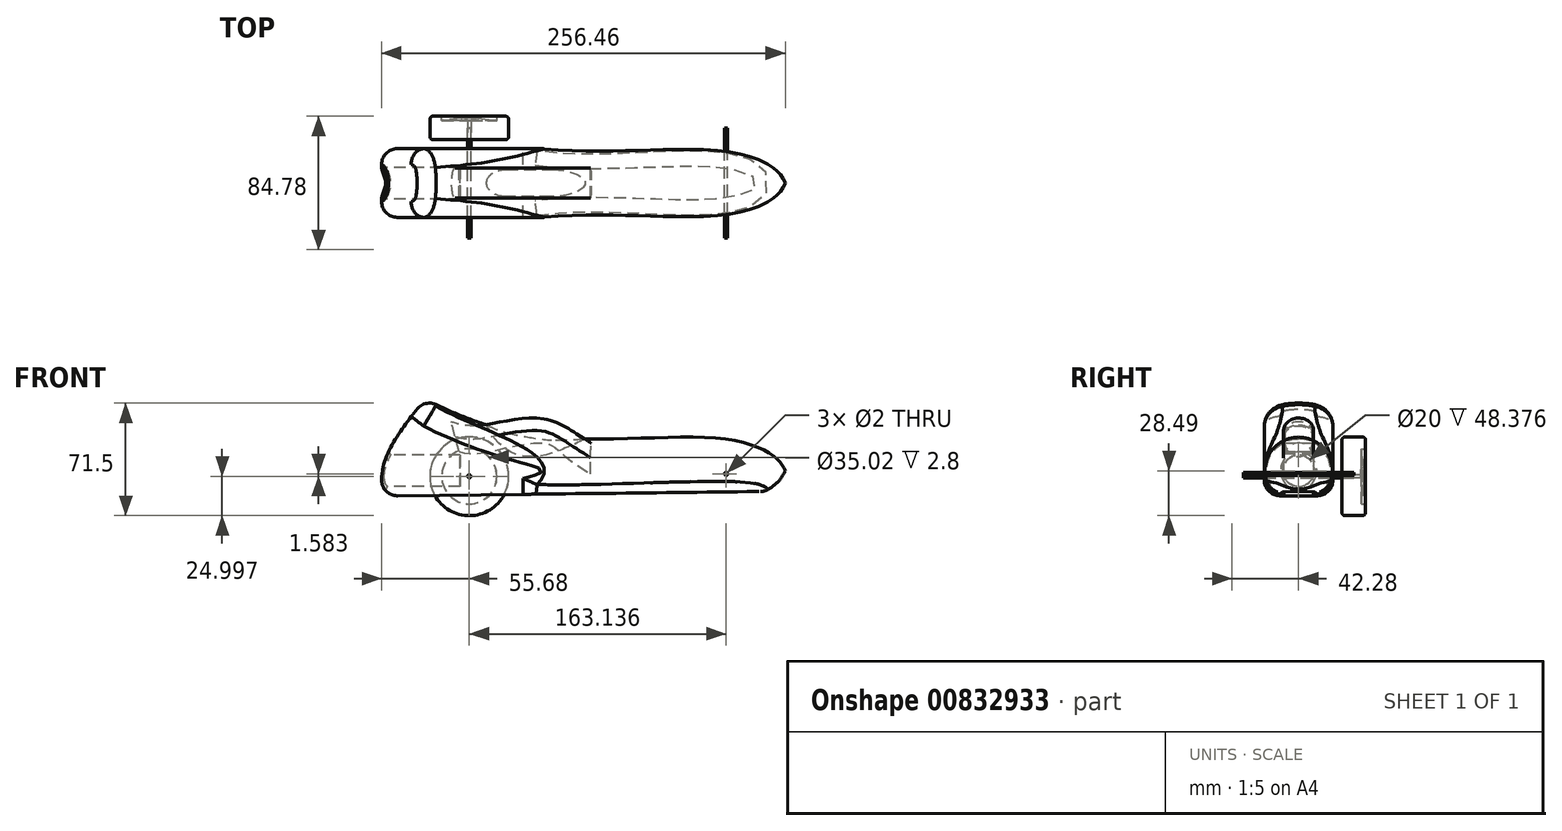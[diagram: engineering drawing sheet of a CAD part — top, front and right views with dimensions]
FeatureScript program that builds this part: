
annotation { "Feature Type Name" : "Feature", "Feature Type Description" : "" }
export const myFeature = defineFeature(function(context is Context, id is Id, definition is map)
    precondition{}
    {
        {
            var Q0;
            Q0=qCreatedBy(makeId("Front.planeOp"),FACE);
            var sketch = newSketch(context, id + "F0", { "sketchPlane" : qUnion([Q0])});
            skLineSegment(sketch, "E0", {"start": v(-118.32, 0) * mm, "end": v(131.68, 0) * mm, "construction": true});
            skFitSpline(sketch, "E1", {"points": [v(131.68, 0) * mm, v(126.03, 7.94) * mm, v(93, 20.22) * mm, v(-29.78, 22.76) * mm, v(-128.5, 62.65) * mm], "startDerivative": vector(-40.38, 77.18) * mm, "endDerivative": vector(-267.3, 151.76) * mm});
            skLineSegment(sketch, "E2", {"start": v(-128.5, 62.65) * mm, "end": v(-128.5, 0) * mm});
            skLineSegment(sketch, "E3", {"start": v(-128.5, 0) * mm, "end": v(131.68, 0) * mm});
            skSolve(sketch);
        }
        {
            var Q0;
            Q0 = qSketchRegion(id + "F0", true);
            var Q1;
            Q1=sQuery(id+"F0.wireOp",EDGE,"E3");
            revolve(context, id + "F1", {"surfaceOperationType" : NewSurfaceOperationType.NEW, "entities" : qUnion([Q0]), "axis" : qUnion([Q1]), "revolveType" : RevolveType.FULL});
        }
        {
            var Q0;
            Q0=qCreatedBy(makeId("Front.planeOp"),FACE);
            var sketch = newSketch(context, id + "F2", { "sketchPlane" : qUnion([Q0])});
            skLineSegment(sketch, "E4", {"start": v(129, -13) * mm, "end": v(-152.67, -16.28) * mm});
            skLineSegment(sketch, "E5", {"start": v(-152.67, -16.28) * mm, "end": v(-151.96, -77.92) * mm});
            skLineSegment(sketch, "E6", {"start": v(-151.96, -77.92) * mm, "end": v(124.08, -74.71) * mm});
            skLineSegment(sketch, "E7", {"start": v(124.08, -74.71) * mm, "end": v(129, -13) * mm});
            skSolve(sketch);
        }
        {
            var Q0;
            Q0=makeQuery(id+"F2.imprint","IMPRINT",FACE,{"disambiguationData":[TD([[makeQuery(id+"F2.imprint","IMPRINT",EDGE,{"derivedFrom":sQuery(id+"F2.wireOp",EDGE,"E4")}),1.0]])]});
            extrude(context, id + "F3", {"entities" : qUnion([Q0]), "operationType" : NewBodyOperationType.REMOVE, "endBound" : BoundingType.THROUGH_ALL, "oppositeDirection" : true, "depth" : 25 * mm, "offsetDistance" : 25 * mm, "hasSecondDirection" : true, "secondDirectionBound" : BoundingType.THROUGH_ALL, "secondDirectionOppositeDirection" : false, "secondDirectionDepth" : 25 * mm});
        }
        {
            var Q0;
            Q0=qCreatedBy(makeId("Right.planeOp"),FACE);
            var sketch = newSketch(context, id + "F4", { "sketchPlane" : qUnion([Q0])});
            skLineSegment(sketch, "E8", {"start": v(21.79, -20.57) * mm, "end": v(21.79, 59.86) * mm});
            skLineSegment(sketch, "E9", {"start": v(21.79, 59.86) * mm, "end": v(72.66, 59.86) * mm});
            skLineSegment(sketch, "E10", {"start": v(72.66, 59.86) * mm, "end": v(72.66, -20.57) * mm});
            skLineSegment(sketch, "E11", {"start": v(72.66, -20.57) * mm, "end": v(21.46, -20.57) * mm});
            skLineSegment(sketch, "E12.MirrorCS", {"start": v(-21.79, -20.57) * mm, "end": v(-21.79, 59.86) * mm});
            skLineSegment(sketch, "E13.MirrorCS", {"start": v(-21.79, 59.86) * mm, "end": v(-72.66, 59.86) * mm});
            skLineSegment(sketch, "E14.MirrorCS", {"start": v(-72.66, 59.86) * mm, "end": v(-72.66, -20.57) * mm});
            skLineSegment(sketch, "E15.MirrorCS", {"start": v(-72.66, -20.57) * mm, "end": v(-21.46, -20.57) * mm});
            skSolve(sketch);
        }
        {
            var Q0;
            {var subQ0=sQuery(id+"F4.wireOp",EDGE,"E12.MirrorCS");Q0=makeQuery(id+"F4.imprint","IMPRINT",FACE,{"disambiguationData":[TD([[makeQuery(id+"F4.imprint","IMPRINT",EDGE,{"derivedFrom":subQ0}),1.0]])]});}
            var Q1;
            {var subQ0=sQuery(id+"F4.wireOp",EDGE,"E8");Q1=makeQuery(id+"F4.imprint","IMPRINT",FACE,{"disambiguationData":[TD([[makeQuery(id+"F4.imprint","IMPRINT",EDGE,{"derivedFrom":subQ0}),-1.0]])]});}
            extrude(context, id + "F5", {"entities" : qUnion([Q0, Q1]), "operationType" : NewBodyOperationType.REMOVE, "endBound" : BoundingType.THROUGH_ALL, "oppositeDirection" : true, "depth" : 25 * mm, "offsetDistance" : 25 * mm});
        }
        {
            var Q0;
            Q0=makeQuery(id+"F5.boolean.opBoolean","INTERSECT",EDGE,{"derivedFrom":[makeQuery(id+"F1.opRevolve","SWEPT_FACE",FACE,{"disambiguationData":[OSD([sQuery(id+"F0.wireOp",EDGE,"E1")])]}),makeQuery(id+"F5.opExtrude","SWEPT_FACE",FACE,{"disambiguationData":[OSD([sQuery(id+"F4.wireOp",EDGE,"E12.MirrorCS")])]})]});
            var Q1;
            Q1=makeQuery(id+"F5.boolean.opBoolean","INTERSECT",EDGE,{"derivedFrom":[makeQuery(id+"F1.opRevolve","SWEPT_FACE",FACE,{"disambiguationData":[OSD([sQuery(id+"F0.wireOp",EDGE,"E1")])]}),makeQuery(id+"F5.opExtrude","SWEPT_FACE",FACE,{"disambiguationData":[OSD([sQuery(id+"F4.wireOp",EDGE,"E8")])]})]});
            fillet(context, id + "F6", {"entities" : qUnion([Q0, Q1]), "radius" : 15 * mm, "tangentPropagation" : true, "allowEdgeOverflow" : false});
        }
        {
            var Q0;
            Q0=qCreatedBy(makeId("Front.planeOp"),FACE);
            var sketch = newSketch(context, id + "F7", { "sketchPlane" : qUnion([Q0])});
            skFitSpline(sketch, "E16", {"points": [v(-121.86, -24.45) * mm, v(-123.5, 3.78) * mm, v(-90.97, 53.08) * mm], "startDerivative": vector(-16.07, 66.09) * mm, "endDerivative": vector(72.48, 87.66) * mm});
            skLineSegment(sketch, "E17", {"start": v(-90.97, 53.08) * mm, "end": v(-135.15, 76.81) * mm});
            skLineSegment(sketch, "E18", {"start": v(-135.15, 76.81) * mm, "end": v(-154.59, -23.22) * mm});
            skLineSegment(sketch, "E19", {"start": v(-154.59, -23.22) * mm, "end": v(-122.27, -35.5) * mm});
            skLineSegment(sketch, "E20", {"start": v(-122.27, -35.5) * mm, "end": v(-121.86, -24.45) * mm});
            skSolve(sketch);
        }
        {
            var Q0;
            Q0=makeQuery(id+"F7.imprint","IMPRINT",FACE,{"disambiguationData":[TD([[makeQuery(id+"F7.imprint","IMPRINT",EDGE,{"derivedFrom":sQuery(id+"F7.wireOp",EDGE,"E16")}),1.0]])]});
            extrude(context, id + "F8", {"entities" : qUnion([Q0]), "operationType" : NewBodyOperationType.REMOVE, "endBound" : BoundingType.THROUGH_ALL, "oppositeDirection" : true, "depth" : 25 * mm, "offsetDistance" : 25 * mm, "hasSecondDirection" : true, "secondDirectionBound" : BoundingType.THROUGH_ALL, "secondDirectionOppositeDirection" : false, "secondDirectionDepth" : 25 * mm});
        }
        {
            var Q0;
            Q0=makeQuery(id+"F8.boolean.opBoolean","INTERSECT",EDGE,{"derivedFrom":[makeQuery(id+"F5.boolean.opBoolean","COPY",FACE,{"derivedFrom":makeQuery(id+"F5.opExtrude","SWEPT_FACE",FACE,{"disambiguationData":[OSD([sQuery(id+"F4.wireOp",EDGE,"E12.MirrorCS")])]})}),makeQuery(id+"F8.opExtrude","SWEPT_FACE",FACE,{"disambiguationData":[OSD([sQuery(id+"F7.wireOp",EDGE,"E16")])]})]});
            fillet(context, id + "F9", {"entities" : qUnion([Q0]), "radius" : 10 * mm, "tangentPropagation" : true, "allowEdgeOverflow" : false});
        }
        {
            var Q0;
            Q0=makeQuery(id+"F5.boolean.opBoolean","INTERSECT",EDGE,{"derivedFrom":[makeQuery(id+"F3.boolean.opBoolean","COPY",FACE,{"derivedFrom":makeQuery(id+"F3.opExtrude","SWEPT_FACE",FACE,{"disambiguationData":[OSD([sQuery(id+"F2.wireOp",EDGE,"E4")])]})}),makeQuery(id+"F5.opExtrude","SWEPT_FACE",FACE,{"disambiguationData":[OSD([sQuery(id+"F4.wireOp",EDGE,"E8")])]})]});
            fillet(context, id + "F10", {"entities" : qUnion([Q0]), "radius" : 10 * mm, "tangentPropagation" : true, "allowEdgeOverflow" : false});
        }
        {
            var Q0;
            Q0=qCreatedBy(makeId("Right.planeOp"),FACE);
            cPlane(context, id + "F11", {"entities" : qUnion([Q0]), "cplaneType" : CPlaneType.OFFSET, "offset" : 124.9 * mm, "oppositeDirection" : true, "width" : 150 * mm, "height" : 150 * mm});
        }
        {
            var Q0;
            Q0=qCreatedBy(id+"F11.planeOp",FACE);
            var sketch = newSketch(context, id + "F12", { "sketchPlane" : qUnion([Q0])});
            skCircle(sketch, "E21", {"center": v(0, 0) * mm, "radius": 10 * mm});
            skSolve(sketch);
        }
        {
            var Q0;
            Q0=makeQuery(id+"F12.imprint","IMPRINT",FACE,{"disambiguationData":[TD([[makeQuery(id+"F12.imprint","IMPRINT",EDGE,{"derivedFrom":sQuery(id+"F12.wireOp",EDGE,"E21")}),1.0]])]});
            extrude(context, id + "F13", {"entities" : qUnion([Q0]), "operationType" : NewBodyOperationType.REMOVE, "depth" : 50 * mm, "offsetDistance" : 25 * mm});
        }
        {
            var Q0;
            Q0=makeQuery(id+"F13.boolean.opBoolean","INTERSECT",EDGE,{"derivedFrom":[makeQuery(id+"F8.boolean.opBoolean","COPY",FACE,{"derivedFrom":makeQuery(id+"F8.opExtrude","SWEPT_FACE",FACE,{"disambiguationData":[OSD([sQuery(id+"F7.wireOp",EDGE,"E16")])]})}),makeQuery(id+"F13.opExtrude","SWEPT_FACE",FACE,{"disambiguationData":[OSD([sQuery(id+"F12.wireOp",EDGE,"E21")])]})]});
            var Q1;
            Q1=makeQuery(id+"F13.boolean.opBoolean","INTERSECT",EDGE,{"derivedFrom":[makeQuery(id+"F10.opFillet","BLEND_FACE",FACE,{"disambiguationData":[OSD([sQuery(id+"F2.wireOp",EDGE,"E4"),sQuery(id+"F7.wireOp",EDGE,"E16")])]}),makeQuery(id+"F13.opExtrude","SWEPT_FACE",FACE,{"disambiguationData":[OSD([sQuery(id+"F12.wireOp",EDGE,"E21")])]})]});
            chamfer(context, id + "F14", {"entities" : qUnion([Q0, Q1]), "width" : 1.5 * mm, "tangentPropagation" : true});
        }
        {
            var Q0;
            Q0=qCreatedBy(makeId("Front.planeOp"),FACE);
            var sketch = newSketch(context, id + "F15", { "sketchPlane" : qUnion([Q0])});
            skLineSegment(sketch, "E22", {"start": v(-81.16, -3.61) * mm, "end": v(140.1, -1.46) * mm, "construction": true});
            skCircle(sketch, "E23", {"center": v(94.04, -1.91) * mm, "radius": 1 * mm});
            skCircle(sketch, "E24", {"center": v(-69.1, -3.5) * mm, "radius": 1 * mm});
            skSolve(sketch);
        }
        {
            var Q0;
            Q0 = qSketchRegion(id + "F15", true);
            extrude(context, id + "F16", {"entities" : qUnion([Q0]), "operationType" : NewBodyOperationType.REMOVE, "endBound" : BoundingType.THROUGH_ALL, "depth" : 25 * mm, "offsetDistance" : 25 * mm, "hasSecondDirection" : true, "secondDirectionBound" : BoundingType.THROUGH_ALL, "secondDirectionOppositeDirection" : true, "secondDirectionDepth" : 25 * mm});
        }
        {
            var Q0;
            Q0 = qSketchRegion(id + "F15", true);
            extrude(context, id + "F17", {"entities" : qUnion([Q0]), "depth" : 35 * mm, "offsetDistance" : 25 * mm, "hasSecondDirection" : true, "secondDirectionOppositeDirection" : true, "secondDirectionDepth" : 35 * mm});
        }
        {
            var Q0;
            Q0=makeQuery(id+"F17.opExtrude","CAP_FACE",FACE,{"disambiguationData":[OSD([sQuery(id+"F15.wireOp",EDGE,"E24")])],"isStart":true});
            var sketch = newSketch(context, id + "F18", { "sketchPlane" : qUnion([Q0])});
            skCircle(sketch, "E25", {"center": v(69.1, -3.5) * mm, "radius": 25 * mm});
            skSolve(sketch);
        }
        {
            var Q0;
            Q0=makeQuery(id+"F18.imprint","IMPRINT",FACE,{"disambiguationData":[TD([[makeQuery(id+"F18.imprint","IMPRINT",EDGE,{"derivedFrom":sQuery(id+"F18.wireOp",EDGE,"E25")}),1.0]])]});
            extrude(context, id + "F19", {"entities" : qUnion([Q0]), "depth" : 15 * mm, "offsetDistance" : 25 * mm, "symmetric" : true});
        }
        {
            var Q0;
            Q0=makeQuery(id+"F19.opExtrude","CAP_FACE",FACE,{"disambiguationData":[OSD([sQuery(id+"F15.wireOp",EDGE,"E24"),sQuery(id+"F18.wireOp",EDGE,"E25")])],"isStart":false});
            var sketch = newSketch(context, id + "F20", { "sketchPlane" : qUnion([Q0])});
            skCircle(sketch, "E26", {"center": v(69.1, -3.5) * mm, "radius": 17.5 * mm});
            skSolve(sketch);
        }
        {
            var Q0;
            Q0=makeQuery(id+"F20.imprint","IMPRINT",FACE,{"disambiguationData":[TD([[makeQuery(id+"F20.imprint","IMPRINT",EDGE,{"derivedFrom":sQuery(id+"F20.wireOp",EDGE,"E26")}),1.0]])]});
            extrude(context, id + "F21", {"entities" : qUnion([Q0]), "operationType" : NewBodyOperationType.REMOVE, "oppositeDirection" : true, "depth" : 2.8 * mm, "offsetDistance" : 25 * mm});
        }
        {
            var Q0;
            Q0=makeQuery(id+"F21.boolean.opBoolean","COPY",EDGE,{"derivedFrom":makeQuery(id+"F21.opExtrude","CAP_EDGE",EDGE,{"disambiguationData":[OSD([sQuery(id+"F20.wireOp",EDGE,"E26")])],"isStart":true})});
            var Q1;
            Q1=makeQuery(id+"F19.opExtrude","CAP_EDGE",EDGE,{"disambiguationData":[OSD([sQuery(id+"F18.wireOp",EDGE,"E25")])],"isStart":false});
            var Q2;
            Q2=makeQuery(id+"F19.opExtrude","CAP_EDGE",EDGE,{"disambiguationData":[OSD([sQuery(id+"F18.wireOp",EDGE,"E25")])],"isStart":true});
            fillet(context, id + "F22", {"entities" : qUnion([Q0, Q1, Q2]), "radius" : 2 * mm, "tangentPropagation" : true, "allowEdgeOverflow" : false});
        }
        {
            var Q0;
            Q0=qCreatedBy(makeId("Top.planeOp"),FACE);
            cPlane(context, id + "F23", {"entities" : qUnion([Q0]), "cplaneType" : CPlaneType.OFFSET, "offset" : 3.5 * mm, "oppositeDirection" : true, "width" : 150 * mm, "height" : 150 * mm});
        }
        {
            var Q0;
            Q0=qCreatedBy(id+"F23.planeOp",FACE);
            var sketch = newSketch(context, id + "F24", { "sketchPlane" : qUnion([Q0])});
            skLineSegment(sketch, "E27", {"start": v(-51.54, 39.75) * mm, "end": v(-67.92, 41.8) * mm});
            skLineSegment(sketch, "E28", {"start": v(-68.3, 39.66) * mm, "end": v(-67.92, 41.8) * mm});
            skLineSegment(sketch, "E29", {"start": v(-68.3, 39.66) * mm, "end": v(-51.54, 39.75) * mm});
            skLineSegment(sketch, "E30", {"start": v(-69.06, 35.08) * mm, "end": v(-69.06, 45.18) * mm, "construction": true});
            skSolve(sketch);
        }
        {
            var Q0;
            Q0 = qSketchRegion(id + "F24", true);
            var Q1;
            Q1=sQuery(id+"F24.wireOp",EDGE,"E30");
            revolve(context, id + "F25", {"surfaceOperationType" : NewSurfaceOperationType.NEW, "entities" : qUnion([Q0]), "axis" : qUnion([Q1]), "revolveType" : RevolveType.FULL});
        }
        {
            var Q0;
            Q0=makeQuery(id+"F25.opRevolve","SWEPT_EDGE",EDGE,{"disambiguationData":[OSD([sQuery(id+"F24.wireOp",EDGE,"E27"),sQuery(id+"F24.wireOp",EDGE,"E28")])]});
            fillet(context, id + "F26", {"entities" : qUnion([Q0]), "radius" : 5 * mm, "tangentPropagation" : true, "allowEdgeOverflow" : false});
        }
        {
            var Q0;
            Q0=qCreatedBy(makeId("Front.planeOp"),FACE);
            var sketch = newSketch(context, id + "F27", { "sketchPlane" : qUnion([Q0])});
            skFitSpline(sketch, "E31", {"points": [v(12.04, 32.77) * mm, v(-25.2, 17.09) * mm, v(-43.84, 21.99) * mm, v(-57.56, 47.8) * mm], "startDerivative": vector(-100.83, -53.7) * mm, "endDerivative": vector(-34.57, 90.8) * mm});
            skSolve(sketch);
        }
        {
            var Q0;
            Q0=qCreatedBy(makeId("Right.planeOp"),FACE);
            var sketch = newSketch(context, id + "F28", { "sketchPlane" : qUnion([Q0])});
            skArc(sketch, "E32", {"start": v(-8.61, 26.84) * mm, "mid": v(0, 18.06) * mm, "end": v(8.61, 26.84) * mm});
            skLineSegment(sketch, "E33", {"start": v(-8.61, 26.84) * mm, "end": v(-8.37, 39.02) * mm});
            skLineSegment(sketch, "E34", {"start": v(8.61, 26.84) * mm, "end": v(8.37, 39) * mm});
            skLineSegment(sketch, "E35", {"start": v(8.37, 39) * mm, "end": v(-8.37, 39.02) * mm});
            skSolve(sketch);
        }
        {
            var Q0;
            Q0=makeQuery(id+"F28.imprint","IMPRINT",FACE,{"disambiguationData":[TD([[makeQuery(id+"F28.imprint","IMPRINT",EDGE,{"derivedFrom":sQuery(id+"F28.wireOp",EDGE,"E32")}),1.0]])]});
            var Q1;
            Q1=sQuery(id+"F27.wireOp",EDGE,"E31");
            sweep(context, id + "F29", {"operationType" : NewBodyOperationType.REMOVE, "profiles" : qUnion([Q0]), "path" : qUnion([Q1])});
        }
        {
            var Q0;
            Q0=qCreatedBy(makeId("Right.planeOp"),FACE);
            var sketch = newSketch(context, id + "F30", { "sketchPlane" : qUnion([Q0])});
            skArc(sketch, "E36", {"start": v(9.54, 13.44) * mm, "mid": v(0, 22.99) * mm, "end": v(-9.54, 13.44) * mm});
            skLineSegment(sketch, "E37", {"start": v(9.54, 13.44) * mm, "end": v(9.54, 3.35) * mm});
            skLineSegment(sketch, "E38", {"start": v(-9.54, 3.35) * mm, "end": v(-9.54, 13.44) * mm});
            skLineSegment(sketch, "E39", {"start": v(-9.54, 3.35) * mm, "end": v(9.54, 3.35) * mm});
            skSolve(sketch);
        }
        {
            var Q0;
            Q0=qCreatedBy(makeId("Front.planeOp"),FACE);
            var sketch = newSketch(context, id + "F31", { "sketchPlane" : qUnion([Q0])});
            skFitSpline(sketch, "E40", {"points": [v(8.14, 16.84) * mm, v(-4.5, 24.95) * mm, v(-26.35, 32.78) * mm, v(-65.37, 27.97) * mm, v(-80.35, 30.3) * mm], "startDerivative": vector(-58.37, 38.53) * mm, "endDerivative": vector(-61.48, 19.47) * mm});
            skSolve(sketch);
        }
        {
            var Q0;
            Q0=makeQuery(id+"F30.imprint","IMPRINT",FACE,{"disambiguationData":[TD([[makeQuery(id+"F30.imprint","IMPRINT",EDGE,{"derivedFrom":sQuery(id+"F30.wireOp",EDGE,"E36")}),1.0]])]});
            var Q1;
            Q1=sQuery(id+"F31.wireOp",EDGE,"E40");
            sweep(context, id + "F32", {"profiles" : qUnion([Q0]), "path" : qUnion([Q1])});
        }
    });
